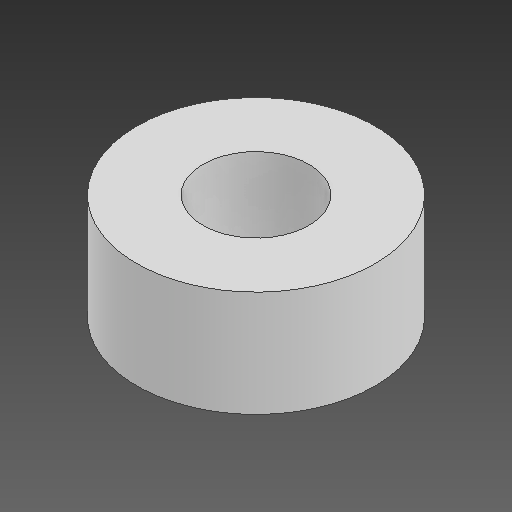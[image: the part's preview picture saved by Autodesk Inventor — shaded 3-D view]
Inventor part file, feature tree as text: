
AUTODESK INVENTOR PART (.ipt)
format: ipt  version: 2021 (Build 250183000, 183)  size: 87,552 bytes
history: native  units: in
note: dims shown in document units (in); Inventor stores cm internally (conversion verified against a paired STEP export)
features: other x3, sketch x1
ambient origin geometry x8: Origin, YZ Plane, XZ Plane, XY Plane, X Axis, Y Axis, Z Axis, Center Point
bodies: Solid1 (feature_tree)
feature tree (4):
  other  "bearing494.ipt"
  other  "Solid1::bearing494.ipt"
  other  "TaggingFeature1"
  sketch  "Sketch1"  dims[d0=0.3937in]
